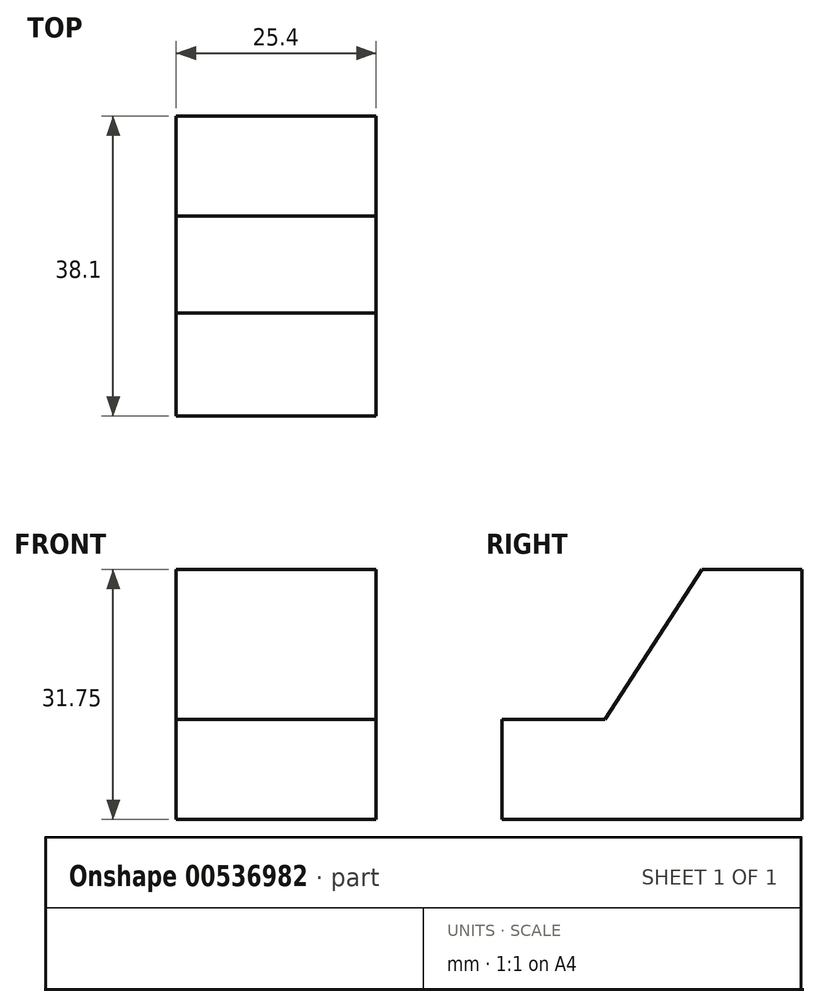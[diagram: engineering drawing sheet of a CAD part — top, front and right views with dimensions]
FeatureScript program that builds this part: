
annotation { "Feature Type Name" : "Feature", "Feature Type Description" : "" }
export const myFeature = defineFeature(function(context is Context, id is Id, definition is map)
    precondition{}
    {
        {
            var Q0;
            Q0=qCreatedBy(makeId("Front.planeOp"),FACE);
            var sketch = newSketch(context, id + "F0", { "sketchPlane" : qUnion([Q0])});
            skLineSegment(sketch, "E0", {"start": v(-62.62, 46.9) * mm, "end": v(-62.62, 14.98) * mm});
            skLineSegment(sketch, "E1", {"start": v(-62.62, 15.15) * mm, "end": v(-37.22, 15.15) * mm});
            skLineSegment(sketch, "E2", {"start": v(-37.22, 15.15) * mm, "end": v(-37.22, 46.9) * mm});
            skLineSegment(sketch, "E3", {"start": v(-37.22, 46.9) * mm, "end": v(-62.62, 46.9) * mm});
            skSolve(sketch);
        }
        {
            var Q0;
            {var subQ2=sQuery(id+"F0.wireOp",EDGE,"E1");Q0=makeQuery(id+"F0.imprint","IMPRINT",FACE,{"disambiguationData":[TD([[makeQuery(id+"F0.imprint","IMPRINT",EDGE,{"derivedFrom":subQ2}),1.0]])]});}
            extrude(context, id + "F1", {"entities" : qUnion([Q0]), "depth" : 38.1 * mm, "offsetDistance" : 25.4 * mm});
        }
        {
            var Q0;
            Q0=makeQuery(id+"F1.opExtrude","SWEPT_FACE",FACE,{"disambiguationData":[OSD([sQuery(id+"F0.wireOp",EDGE,"E0")])]});
            var sketch = newSketch(context, id + "F2", { "sketchPlane" : qUnion([Q0])});
            skLineSegment(sketch, "E4", {"start": v(12.7, 46.9) * mm, "end": v(25.03, 27.85) * mm});
            skLineSegment(sketch, "E5", {"start": v(25.03, 27.85) * mm, "end": v(38.1, 27.85) * mm});
            skSolve(sketch);
        }
        {
            var Q0;
            {var subQ0=sQuery(id+"F2.wireOp",EDGE,"E4");Q0=makeQuery(id+"F2.imprint","IMPRINT",FACE,{"disambiguationData":[TD([[makeQuery(id+"F2.imprint","IMPRINT",EDGE,{"derivedFrom":subQ0}),1.0]])]});}
            extrude(context, id + "F3", {"entities" : qUnion([Q0]), "operationType" : NewBodyOperationType.REMOVE, "endBound" : BoundingType.THROUGH_ALL, "oppositeDirection" : true, "depth" : 25.4 * mm, "offsetDistance" : 25.4 * mm});
        }
    });
